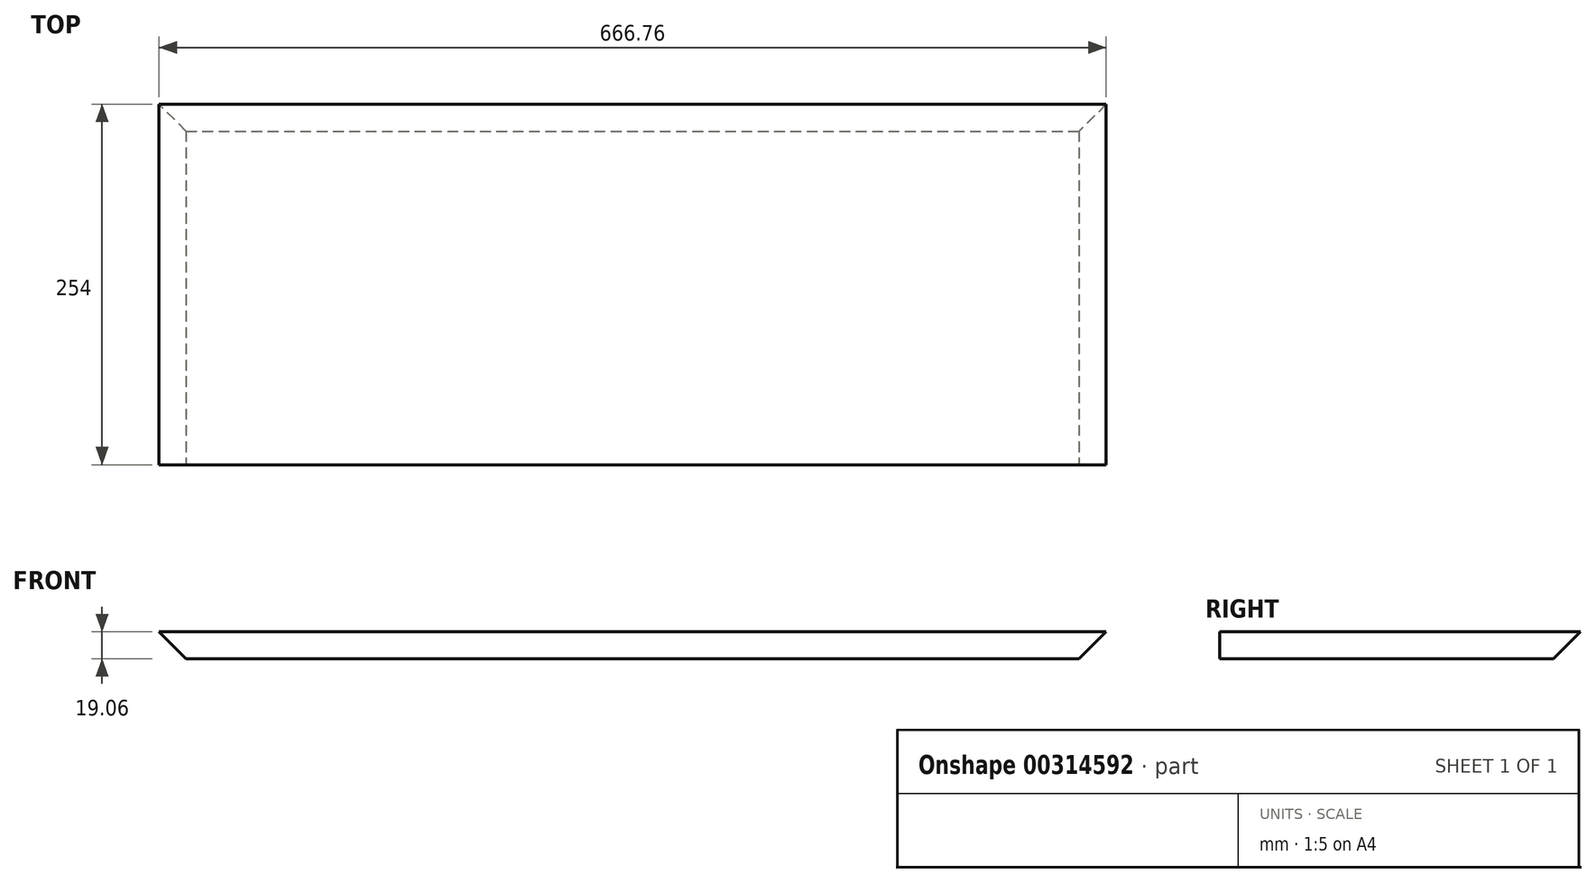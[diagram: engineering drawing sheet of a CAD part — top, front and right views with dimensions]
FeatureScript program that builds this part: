
annotation { "Feature Type Name" : "Feature", "Feature Type Description" : "" }
export const myFeature = defineFeature(function(context is Context, id is Id, definition is map)
    precondition{}
    {
        {
            var Q0;
            Q0=qCreatedBy(makeId("Front.planeOp"),FACE);
            var sketch = newSketch(context, id + "F0", { "sketchPlane" : qUnion([Q0])});
            skLineSegment(sketch, "E0", {"start": v(-333.38, 9.52) * mm, "end": v(333.38, 9.52) * mm});
            skLineSegment(sketch, "E1", {"start": v(333.38, 9.53) * mm, "end": v(314.33, -9.52) * mm});
            skLineSegment(sketch, "E2", {"start": v(314.33, -9.53) * mm, "end": v(-314.33, -9.53) * mm});
            skLineSegment(sketch, "E3", {"start": v(-314.33, -9.53) * mm, "end": v(-333.38, 9.53) * mm});
            skLineSegment(sketch, "E4", {"start": v(0, 9.53) * mm, "end": v(0, -9.53) * mm, "construction": true});
            skSolve(sketch);
        }
        {
            var Q0;
            Q0 = qSketchRegion(id + "F0", true);
            extrude(context, id + "F1", {"entities" : qUnion([Q0]), "oppositeDirection" : true, "depth" : 254 * mm});
        }
        {
            var Q0;
            Q0=makeQuery(id+"F1.opExtrude","CAP_EDGE",EDGE,{"disambiguationData":[OSD([sQuery(id+"F0.wireOp",EDGE,"E2")])],"isStart":false});
            chamfer(context, id + "F2", {"entities" : qUnion([Q0]), "width" : 19.05 * mm, "tangentPropagation" : true});
        }
    });
